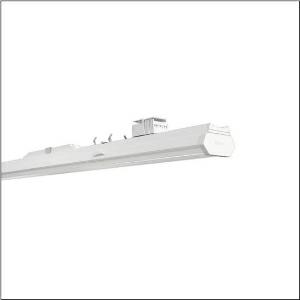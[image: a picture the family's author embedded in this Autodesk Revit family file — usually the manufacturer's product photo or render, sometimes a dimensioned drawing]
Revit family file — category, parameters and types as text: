
# Revit family: licross_r__21_protected_mo_52tp11dn4axg_b280
name_source: partatom
category: Lighting Fixtures
units: mm (PartAtom-declared; Revit-internal decimal feet)

## family parameters
Cut with Voids When Loaded = No
Host = Face
Light Source = No
Part Type = Normal
Room Calculation Point = No
Round Connector Dimension = Use Diameter
Shared = No

## types (1)
- --- (1 x LED, 10000 lm, 57.8 W, 4000K)
    Apparent Load = 58 VA
    CIE Flux Codes = 83 94 98 100 100
    Color Rendering = 80
    Color Temperature = 4000K
    Default Elevation = 1800 mm
    Description = Licross® 21 Protected MO, luminaire insert, of sheet steel, galvanised, coil coated, white, length: 1.500mm, width: 90mm, height: 103mm, LED rated luminous flux: 10.000lm, light colour: 840, control gear: DALI 2, with plug, 5-pole, with phase selection, mains connection: 220..240V, AC, 50/60Hz, rated input power: 58W, halogen-free wiring, primary light control with lens, of plastic, primary optical cover: cover, of PMMA, light emission: direct distribution, primary light characteristic: symmetric, protection rating (complete): IP64, insulation class (complete): insulation class I (protective earthing), certification: CE, ENEC, VDE, UKCA, protection symbol: D if used in an environment with conductive dust loads with corresponding accessories, impact resistance: IK06, permissible ambient temperature for indoor applications: -25..+40°C, corresponds to IFS (International Featured Standards) requirements for safety and quality in the food industry, reducing of maximum allowable ambient temperature of 5°C with ceiling mounting, LABS conformity tested according to VDMA 24364:2018-05, packaging unit: 1 piece
    Height = 92 mm
    Lamp = 1 x LED
    Lamp Light Flux = 10000 lm
    Lamp Power = 57.8 W
    Lamp count = 1
    Length = 1500 mm
    Luminous efficacy = 173 lm/W
    Manufacturer = Siteco
    ModVariant = No
    Model = 52TP11DN4AXG
    Mounting Place = Ceiling
    Mounting Type = Pendant
    Number of Poles = 1
    OnlyDefault = Yes
    Power Factor = 1
    Product Name = Licross® 21 Protected MO
    Product group = luminaire insert
    ProductGroupID = 902
    Protection Class = Protection class I
    Protection Degree = IP 64
    RLX_Detail_Level = 1
    RLX_Emergency_Light_Flux = 0 lm
    RLX_Emergency_Type = 0
    RLX_Emergency_Type_DB = No
    RlxData = <blob elided: 24101 chars, md5=693bb2d3>
    Socket = socket
    Standby Power = 0 W
    System Light Flux = 10000 lm
    System Power = 58 W
    Type Comments = factory setting: luminous flux: 100 % | dim-lin: 254 | 390 mA
    Type Image = l_1256148.jpg
    URL = http://relux.com
    VarID = @adj_128132
    Voltage = 0 V
    Weight = 0.00 kg
    Width = 88 mm

## geometry (parser evidence)
native form markers: Blend x4, Sweep x12
no freeform markers — native parametric forms only
